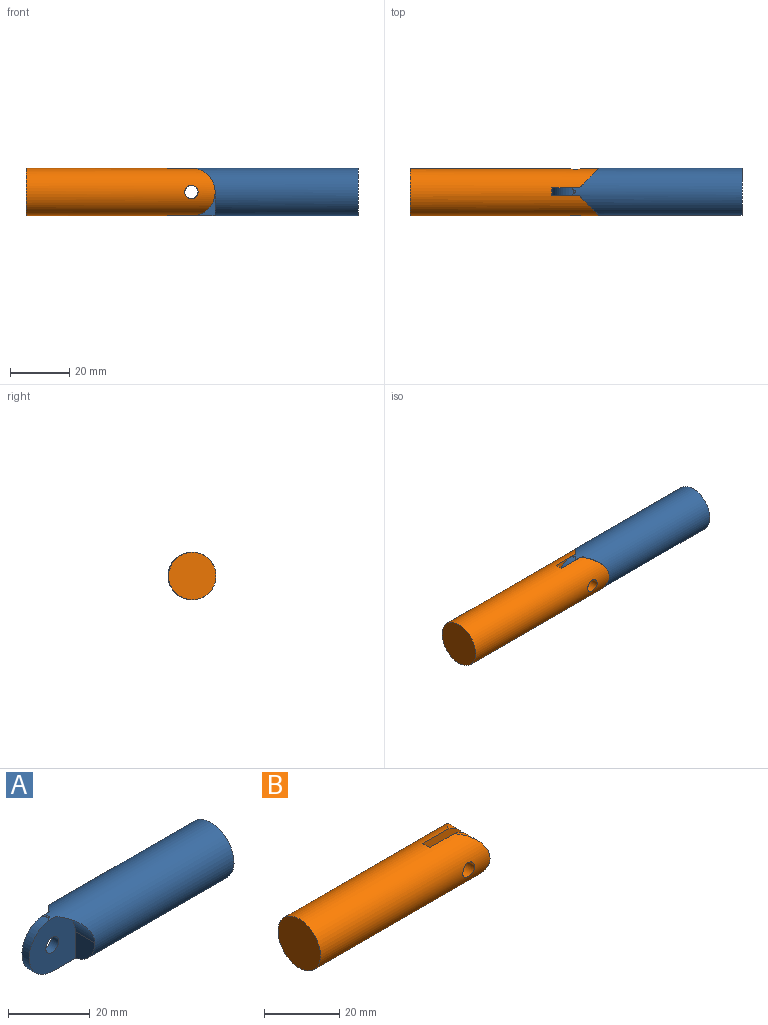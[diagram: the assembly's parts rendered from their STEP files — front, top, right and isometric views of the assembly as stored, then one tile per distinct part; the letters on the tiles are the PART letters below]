
ASSEMBLY  parts=2 mates=1
PART A: 14 faces, bbox 64.3x16x16 mm
  f0: plane 1.36x0.68mm, normal (-0.04,0,1), area 0.6mm2, adj f6,f9
  f1: plane 7.9x6.75mm, normal (-1,0,0), area 40.3mm2, adj f3,f6,f13
  f2: plane 7.9x6.75mm, normal (-1,0,0), area 40.3mm2, adj f4,f6,f12
  f3: plane 16x15.9mm, normal (0,-1,0), area 198.7mm2, adj f1,f6,f8,f9,f10,f11,f13
  f4: plane 16x15.9mm, normal (0,1,0), area 198.7mm2, adj f2,f6,f7,f9,f10,f11,f12
  f5: plane 16x16mm, normal (1,0,0), area 201.1mm2, adj f6
  f6: cylinder r=8mm len=57.57mm, axis (-1,0,0), area 2504.9mm2, adj f0,f1,f2,f3,f4,f5,f7,f8
  f7: plane 1.25x0.1mm, normal (1,0,0), area 0mm2, adj f4,f6,f10
  f8: plane 1.25x0.1mm, normal (1,0,0), area 0mm2, adj f3,f6,f10
  f9: cylinder r=8mm len=15.97mm, axis (0,1,0), area 60.8mm2, adj f0,f3,f4,f6,f10
  f10: plane 8x2.5mm, normal (0,0,-1), area 20mm2, adj f3,f4,f7,f8,f9
  f11: cylinder r=2.25mm len=4.5mm, axis (0,1,0), area 35.3mm2, adj f3,f4
  f12: cylinder r=8mm len=7.9mm, axis (0,1,0), area 49.1mm2, adj f2,f4,f6
  f13: cylinder r=8mm len=7.9mm, axis (0,1,0), area 49.1mm2, adj f1,f3,f6
PART B: 9 faces, bbox 63.9x16x16 mm
  f0: cylinder r=8mm len=63.94mm, axis (1,0,0), area 2987.4mm2, adj f1,f2,f3,f4,f5,f6,f7,f8
  f1: plane 16x15.8mm, normal (0,1,0), area 210.9mm2, adj f0,f3,f6,f8
  f2: plane 16x15.74mm, normal (0,-1,0), area 210.2mm2, adj f0,f3,f5,f7
  f3: plane 16x2.7mm, normal (1,0,0), area 43mm2, adj f0,f1,f2
  f4: plane 16x16mm, normal (-1,0,0), area 201.1mm2, adj f0
  f5: cylinder r=2.25mm len=6.55mm, axis (0,-1,0), area 90.3mm2, adj f0,f2
  f6: cylinder r=2.25mm len=6.75mm, axis (0,-1,0), area 93.2mm2, adj f0,f1
  f7: cylinder r=8mm len=15.74mm, axis (0,-1,0), area 93.7mm2, adj f0,f2
  f8: cylinder r=8mm len=15.8mm, axis (0,-1,0), area 98.1mm2, adj f0,f1
PLACE A t=(39.06,0.2,54.12)mm
PLACE B t=(-14.4,0,18.6)mm
MATE revolute A.f9 <-> B.f5  axis (0,1,0) through (11.7,1.45,18.6)mm
